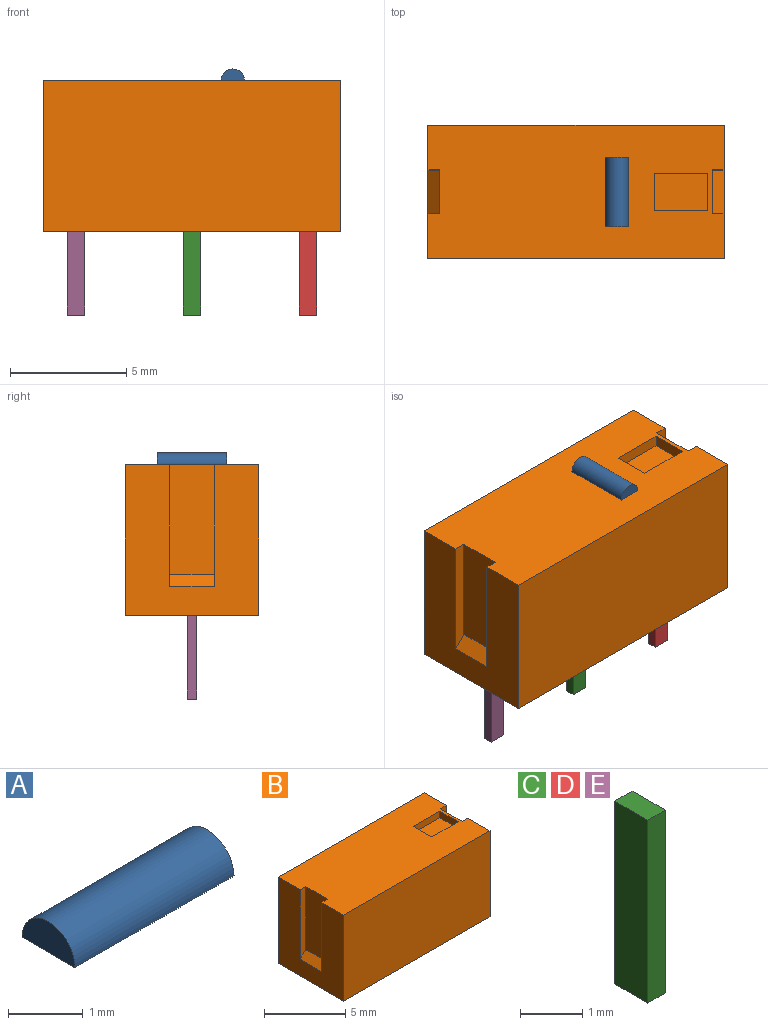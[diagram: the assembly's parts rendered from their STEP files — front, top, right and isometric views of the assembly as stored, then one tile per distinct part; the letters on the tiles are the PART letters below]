
ASSEMBLY  parts=5 mates=4
PART A: 4 faces, bbox 3x1x0.5 mm
  f0: plane 1x0.5mm, normal (1,0,0), area 0.4mm2, adj f2,f3
  f1: plane 1x0.5mm, normal (-1,0,0), area 0.4mm2, adj f2,f3
  f2: plane 3x1mm, normal (0,0,-1), area 3mm2, adj f0,f1,f3
  f3: cylinder r=0.5mm len=3mm, axis (-1,0,0), area 4.7mm2, adj f0,f1,f2
PART B: 19 faces, bbox 12.8x5.8x6.5 mm
  f0: plane 12.75x5.75mm, normal (0,0,1), area 67.7mm2, adj f1,f2,f3,f4,f6,f7,f8,f9
  f1: plane 6.5x5.75mm, normal (1,0,0), area 27.4mm2, adj f0,f2,f4,f5,f9,f11,f13
  f2: plane 12.75x6.5mm, normal (0,1,0), area 82.9mm2, adj f0,f1,f3,f5
  f3: plane 6.5x5.75mm, normal (-1,0,0), area 27.4mm2, adj f0,f2,f4,f5,f7,f8,f12
  f4: plane 12.75x6.5mm, normal (0,-1,0), area 82.9mm2, adj f0,f1,f3,f5
  f5: plane 12.75x5.75mm, normal (0,0,-1), area 73.3mm2, adj f1,f2,f3,f4
  f6: plane 4.75x1.9mm, normal (-1,0,0), area 9mm2, adj f0,f7,f8,f12
  f7: plane 5.25x0.5mm, normal (0,-1,0), area 2.5mm2, adj f0,f3,f6,f12
  f8: plane 5.25x0.5mm, normal (0,1,0), area 2.5mm2, adj f0,f3,f6,f12
  f9: plane 5.25x0.5mm, normal (0,-1,0), area 2.5mm2, adj f0,f1,f10,f13
  f10: plane 4.75x1.9mm, normal (1,0,0), area 9mm2, adj f0,f9,f11,f13
  f11: plane 5.25x0.5mm, normal (0,1,0), area 2.5mm2, adj f0,f1,f10,f13
  f12: plane 1.9x0.5mm, normal (-0.71,0,0.71), area 1.3mm2, adj f3,f6,f7,f8
  f13: plane 1.9x0.5mm, normal (0.71,0,0.71), area 1.3mm2, adj f1,f9,f10,f11
  f14: plane 1.6x0.5mm, normal (-1,0,0), area 0.8mm2, adj f0,f15,f17,f18
  f15: plane 2.3x0.5mm, normal (0,-1,0), area 1.1mm2, adj f0,f14,f16,f18
  f16: plane 1.6x0.5mm, normal (1,0,0), area 0.8mm2, adj f0,f15,f17,f18
  f17: plane 2.3x0.5mm, normal (0,1,0), area 1.1mm2, adj f0,f14,f16,f18
  f18: plane 2.3x1.6mm, normal (0,0,1), area 3.7mm2, adj f14,f15,f16,f17
PART C: 6 faces, bbox 0.4x0.8x3.6 mm
  f0: plane 3.6x0.75mm, normal (1,0,0), area 2.7mm2, adj f1,f3,f4,f5
  f1: plane 3.6x0.4mm, normal (0,1,0), area 1.4mm2, adj f0,f2,f4,f5
  f2: plane 3.6x0.75mm, normal (-1,0,0), area 2.7mm2, adj f1,f3,f4,f5
  f3: plane 3.6x0.4mm, normal (0,-1,0), area 1.4mm2, adj f0,f2,f4,f5
  f4: plane 0.75x0.4mm, normal (0,0,1), area 0.3mm2, adj f0,f1,f2,f3
  f5: plane 0.75x0.4mm, normal (0,0,-1), area 0.3mm2, adj f0,f1,f2,f3
PART D: same geometry as C
PART E: same geometry as C
PLACE A rot(axis=(0,0,1),90deg) t=(0.47,2.05,7.43)mm
PLACE B t=(-1.28,2.05,0.93)mm
PLACE C rot(axis=(0,0,-1),90deg) t=(-1.28,2.05,-2.67)mm
PLACE D rot(axis=(0,0,-1),90deg) t=(3.72,2.05,-2.67)mm
PLACE E rot(axis=(0,0,-1),90deg) t=(-6.28,2.05,-2.67)mm
MATE fastened A.f2 <-> B.f0  axis (0,0,-1) through (0.47,2.05,7.43)mm
MATE fastened C.f4 <-> B.f5  axis (0,0,1) through (-1.28,2.05,0.93)mm
MATE fastened E.f4 <-> B.f5  axis (0,0,1) through (-6.28,2.05,0.93)mm
MATE fastened D.f4 <-> B.f5  axis (0,0,1) through (3.72,2.05,0.93)mm
